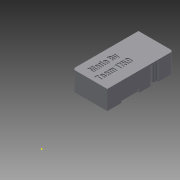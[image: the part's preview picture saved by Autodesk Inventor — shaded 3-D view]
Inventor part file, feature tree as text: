
AUTODESK INVENTOR PART (.ipt)
format: ipt  version: 2015 (Build 190159000, 159)  size: 571,392 bytes
history: native  units: in
note: dims shown in document units (in); Inventor stores cm internally (conversion verified against a paired STEP export)
features: extrude x10, sketch x9, projected_geometry x3, fillet x2, mirror x1
ambient origin geometry x8: Origin, YZ Plane, XZ Plane, XY Plane, X Axis, Y Axis, Z Axis, Center Point
bodies: Solid1 (feature_tree)
feature tree (25):
  extrude  "Extrusion1"  Depth=0.966in
  sketch  "Sketch2"  dims[d5=0.075in d6=0.1in d7=0.1in]
  fillet  "Fillet1"  Radius=0.533in
  fillet  "Fillet2"  Radius=0.075in
  extrude  "Extrusion2"  Depth=0.1in
  extrude  "Extrusion3"  Depth=0.125in
  extrude  "Extrusion4"  Depth=0.1in
  sketch  "Sketch6"  dims[d15=0.1in d16=0.1in]
  extrude  "Extrusion5"  Depth=0.1in
  sketch  "Sketch7"  dims[d17=0.1in d18=0.483in]
  extrude  "Extrusion7"  Depth=0.483in
  extrude  "Extrusion8"  Depth=0.1in
  extrude  "Extrusion9"  Depth=0.1in
  extrude  "Extrusion10"  Depth=0.5in
  mirror  "Mirror1"
  extrude  "Extrusion11"  Depth=0.45in
  sketch  "Sketch1"  dims[d0=1.833in d1=0.966in d2=0.533in d3=0.0in d4=0.075in]
  sketch  "Sketch4"  dims[d8=0.1in d9=0.1in d11=0.125in]
  sketch  "Sketch5"  dims[d13=0.175in d14=0.1in]
  sketch  "Sketch8"  dims[d19=0.0in d20=0.1in]
  projected_geometry  "Projected Loop1"
  sketch  "Sketch9"  dims[d21=0.24in d22=0.1in]
  projected_geometry  "Projected Loop2"
  sketch  "Sketch10"  dims[d23=0.555in d24=0.5in d25=0.45in d26=0.9in d27=0.533in d28=0.0in d29=0.279in d30=0.185in d32=0.3in d33=0.1in d34=0.533in d35=0.0in d36=0.1718in d37=1.2625in d38=0.025in d39=0.0in d40=0.05in d41=0.1in d42=0.025in d43=0.025in d46=0.05in d47=0.025in d48=0.0in d49=0.025in d50=0.0in d51=0.1in d52=0.5in d53=0.05in d54=0.0in d55=0.1in d56=0.0in d57=1.0in d58=0.5in d60=0.375in d61=0.025in d62=0.0in]
  projected_geometry  "Projected Loop3"
